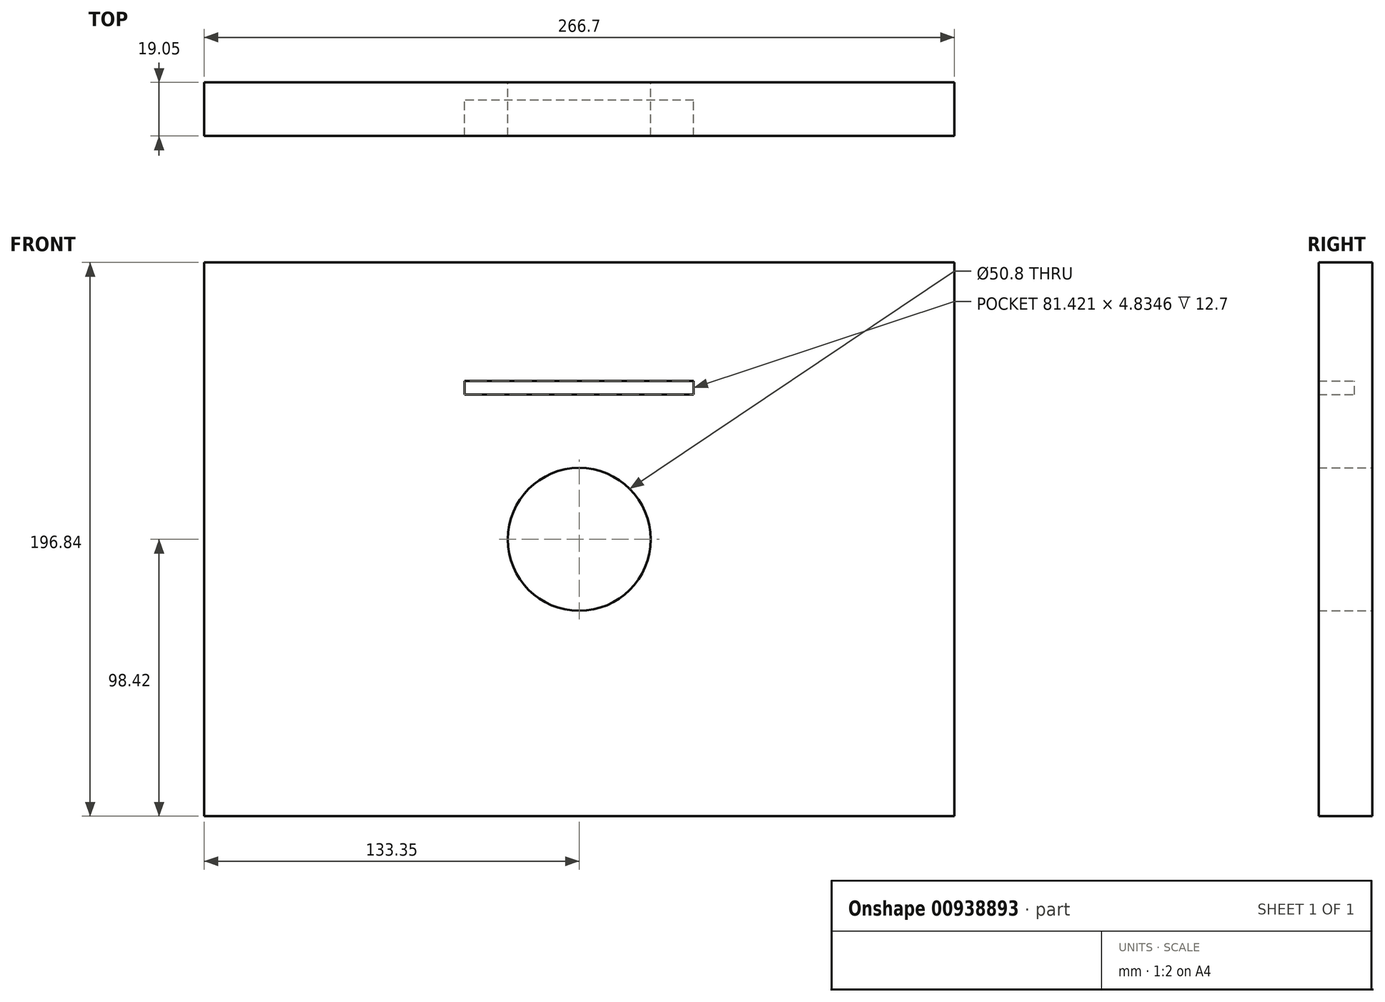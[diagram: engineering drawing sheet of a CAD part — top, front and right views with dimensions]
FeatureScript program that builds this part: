
annotation { "Feature Type Name" : "Feature", "Feature Type Description" : "" }
export const myFeature = defineFeature(function(context is Context, id is Id, definition is map)
    precondition{}
    {
        {
            var Q0;
            Q0=qCreatedBy(makeId("Front.planeOp"),FACE);
            var sketch = newSketch(context, id + "F0", { "sketchPlane" : qUnion([Q0])});
            skLineSegment(sketch, "E0.bottom", {"start": v(133.35, -98.43) * mm, "end": v(-133.35, -98.43) * mm});
            skLineSegment(sketch, "E0.top", {"start": v(133.35, 98.43) * mm, "end": v(-133.35, 98.42) * mm});
            skLineSegment(sketch, "E0.left", {"start": v(133.35, -98.43) * mm, "end": v(133.35, 98.43) * mm});
            skLineSegment(sketch, "E0.right", {"start": v(-133.35, -98.43) * mm, "end": v(-133.35, 98.42) * mm});
            skPoint(sketch, "E0.middle", {"position": v(0, 0) * mm});
            skCircle(sketch, "E1", {"center": v(0, 0) * mm, "radius": 25.4 * mm});
            skLineSegment(sketch, "E2.bottom", {"start": v(40.71, 51.49) * mm, "end": v(-40.71, 51.49) * mm});
            skLineSegment(sketch, "E2.top", {"start": v(40.71, 56.32) * mm, "end": v(-40.71, 56.32) * mm});
            skLineSegment(sketch, "E2.left", {"start": v(40.71, 51.49) * mm, "end": v(40.71, 56.32) * mm});
            skLineSegment(sketch, "E2.right", {"start": v(-40.71, 51.49) * mm, "end": v(-40.71, 56.32) * mm});
            skPoint(sketch, "E2.middle", {"position": v(0, 53.9) * mm});
            skSolve(sketch);
        }
        {
            var Q0;
            Q0 = qSketchRegion(id + "F0", true);
            extrude(context, id + "F1", {"entities" : qUnion([Q0]), "depth" : 19.05 * mm, "offsetDistance" : 25.4 * mm});
        }
        {
            var Q0;
            Q0=makeQuery(id+"F1.opExtrude","CAP_FACE",FACE,{"disambiguationData":[OSD([sQuery(id+"F0.wireOp",EDGE,"E0.bottom"),sQuery(id+"F0.wireOp",EDGE,"E0.top"),sQuery(id+"F0.wireOp",EDGE,"E0.left"),sQuery(id+"F0.wireOp",EDGE,"E0.right"),sQuery(id+"F0.wireOp",EDGE,"E1"),sQuery(id+"F0.wireOp",EDGE,"E2.bottom"),sQuery(id+"F0.wireOp",EDGE,"E2.top"),sQuery(id+"F0.wireOp",EDGE,"E2.left"),sQuery(id+"F0.wireOp",EDGE,"E2.right")])],"isStart":true});
            var sketch = newSketch(context, id + "F2", { "sketchPlane" : qUnion([Q0])});
            skLineSegment(sketch, "E3.bottom", {"start": v(40.71, 51.49) * mm, "end": v(-40.71, 51.49) * mm});
            skLineSegment(sketch, "E3.top", {"start": v(40.71, 56.32) * mm, "end": v(-40.71, 56.32) * mm});
            skLineSegment(sketch, "E3.left", {"start": v(40.71, 51.49) * mm, "end": v(40.71, 56.32) * mm});
            skLineSegment(sketch, "E3.right", {"start": v(-40.71, 51.49) * mm, "end": v(-40.71, 56.32) * mm});
            skSolve(sketch);
        }
        {
            var Q0;
            Q0 = qSketchRegion(id + "F2", true);
            extrude(context, id + "F3", {"entities" : qUnion([Q0]), "operationType" : NewBodyOperationType.ADD, "oppositeDirection" : true, "depth" : 6.35 * mm, "offsetDistance" : 25.4 * mm});
        }
    });
